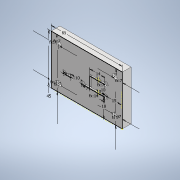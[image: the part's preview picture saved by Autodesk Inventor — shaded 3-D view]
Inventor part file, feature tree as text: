
AUTODESK INVENTOR PART (.ipt)
format: ipt  version: 2021 (Build 250183000, 183)  size: 238,080 bytes
history: native  units: in
note: dims shown in document units (in); Inventor stores cm internally (conversion verified against a paired STEP export)
features: other x7, extrude x4, sketch x3, hole x2, projected_geometry x2
ambient origin geometry x8: Origin, YZ Plane, XZ Plane, XY Plane, X Axis, Y Axis, Z Axis, Center Point
bodies: Solid1 (feature_tree)
feature tree (18):
  other  "points for corner holes and base plate"
  extrude  "Extrusion base plate"  Depth=2.5591in
  other  "plane above base plate to create rib"
  other  "channels and points for valves and for connectors"
  other  "channels as rib"
  extrude  "extrusion of rib to get cutout"  Depth=0.0394in
  sketch  "Sketch6"  dims[d26=1.7717in d27=2.5591in]
  extrude  "valve space extrusion"  Depth=0.2756in
  extrude  "valve bar extrusion"  Depth=0.0512in TaperAngle=0.0deg
  other  "Projected points for every valve"
  other  "all valve spaces"
  other  "projected point for connector holes"
  hole  "holes for connectors"  [1 undecoded]
  hole  "holes for corners"  [1 undecoded]
  sketch  "Sketch7"  dims[d28=0.315in d29=0.0in d30=0.0394in]
  sketch  "Sketch11"  dims[d58=0.0984in d59=0.0689in d60=0.0512in d61=0.0in d62=0.0591in d63=0.1378in d66=0.0787in d67=0.0in d84=0.1614in d85=0.2362in d86=0.1575in d87=0.0787in d88=90.0deg d89=0.0512in d90=0.0in d91=0.2756in d92=0.2756in d93=0.2756in d94=0.2756in d95=0.2756in d96=0.2756in d97=0.2756in d98=0.2756in d99=0.1772in d100=0.2362in d101=0.1575in d102=0.0787in d103=90.0deg d104=0.315in d105=0.0in d106=0.3937in d107=0.5512in d108=0.5512in d109=0.2756in d110=0.3937in d111=0.2756in d116=0.5906in d117=0.7087in d126=0.0394in d127=0.0394in d128=0.0in d129=0.0in d130=0.0394in d131=0.0394in d132=0.2756in d133=0.2756in d134=0.0906in d135=0.0in d136=0.0295in d137=0.0689in d74=0.0197in d75=0.0344in d76=0.0197in d77=0.0344in]
  projected_geometry  "Projected Loop1"
  projected_geometry  "Projected Loop2"
note: 2 required parameter values undecoded (feature->parameter linkage not recoverable at this tier; creation-order binding heuristic only, values carry confidence <= 0.55)
